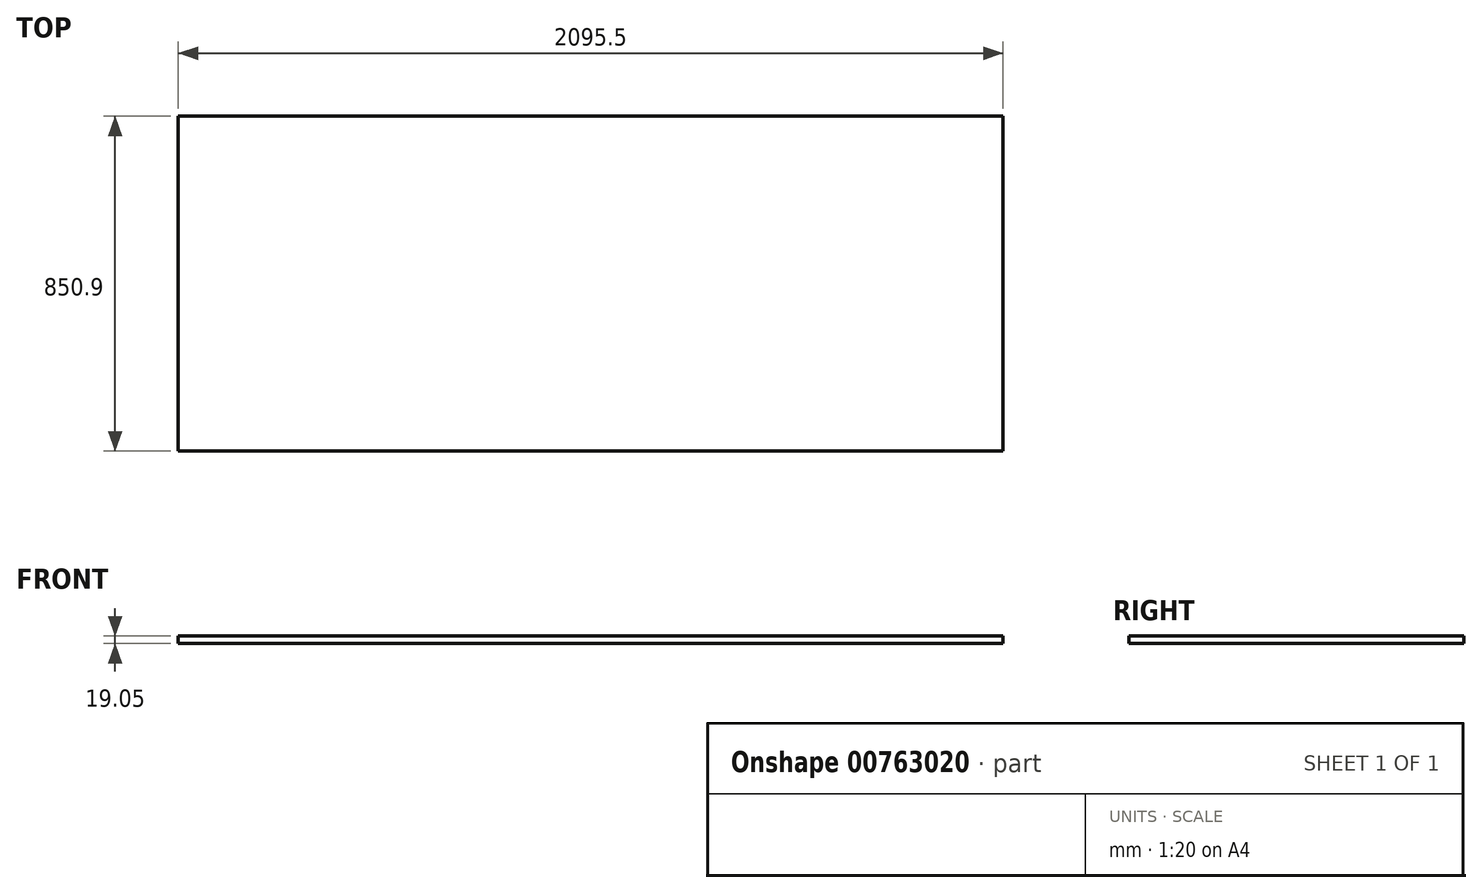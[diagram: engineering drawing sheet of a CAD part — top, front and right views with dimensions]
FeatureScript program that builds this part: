
annotation { "Feature Type Name" : "Feature", "Feature Type Description" : "" }
export const myFeature = defineFeature(function(context is Context, id is Id, definition is map)
    precondition{}
    {
        {
            var Q0;
            Q0=qCreatedBy(makeId("Top.planeOp"),FACE);
            var sketch = newSketch(context, id + "F0", { "sketchPlane" : qUnion([Q0])});
            skLineSegment(sketch, "E0.bottom", {"start": v(-1047.75, 425.45) * mm, "end": v(1047.75, 425.45) * mm});
            skLineSegment(sketch, "E0.top", {"start": v(-1047.75, -425.45) * mm, "end": v(1047.75, -425.45) * mm});
            skLineSegment(sketch, "E0.left", {"start": v(-1047.75, 425.45) * mm, "end": v(-1047.75, -425.45) * mm});
            skLineSegment(sketch, "E0.right", {"start": v(1047.75, 425.45) * mm, "end": v(1047.75, -425.45) * mm});
            skPoint(sketch, "E0.middle", {"position": v(0, 0) * mm});
            skSolve(sketch);
        }
        {
            var Q0;
            Q0=makeQuery(id+"F0.imprint","IMPRINT",FACE,{"disambiguationData":[TD([[makeQuery(id+"F0.imprint","IMPRINT",EDGE,{"derivedFrom":sQuery(id+"F0.wireOp",EDGE,"E0.bottom")}),-1.0]])]});
            extrude(context, id + "F1", {"entities" : qUnion([Q0]), "depth" : 19.05 * mm, "offsetDistance" : 25.4 * mm});
        }
    });
